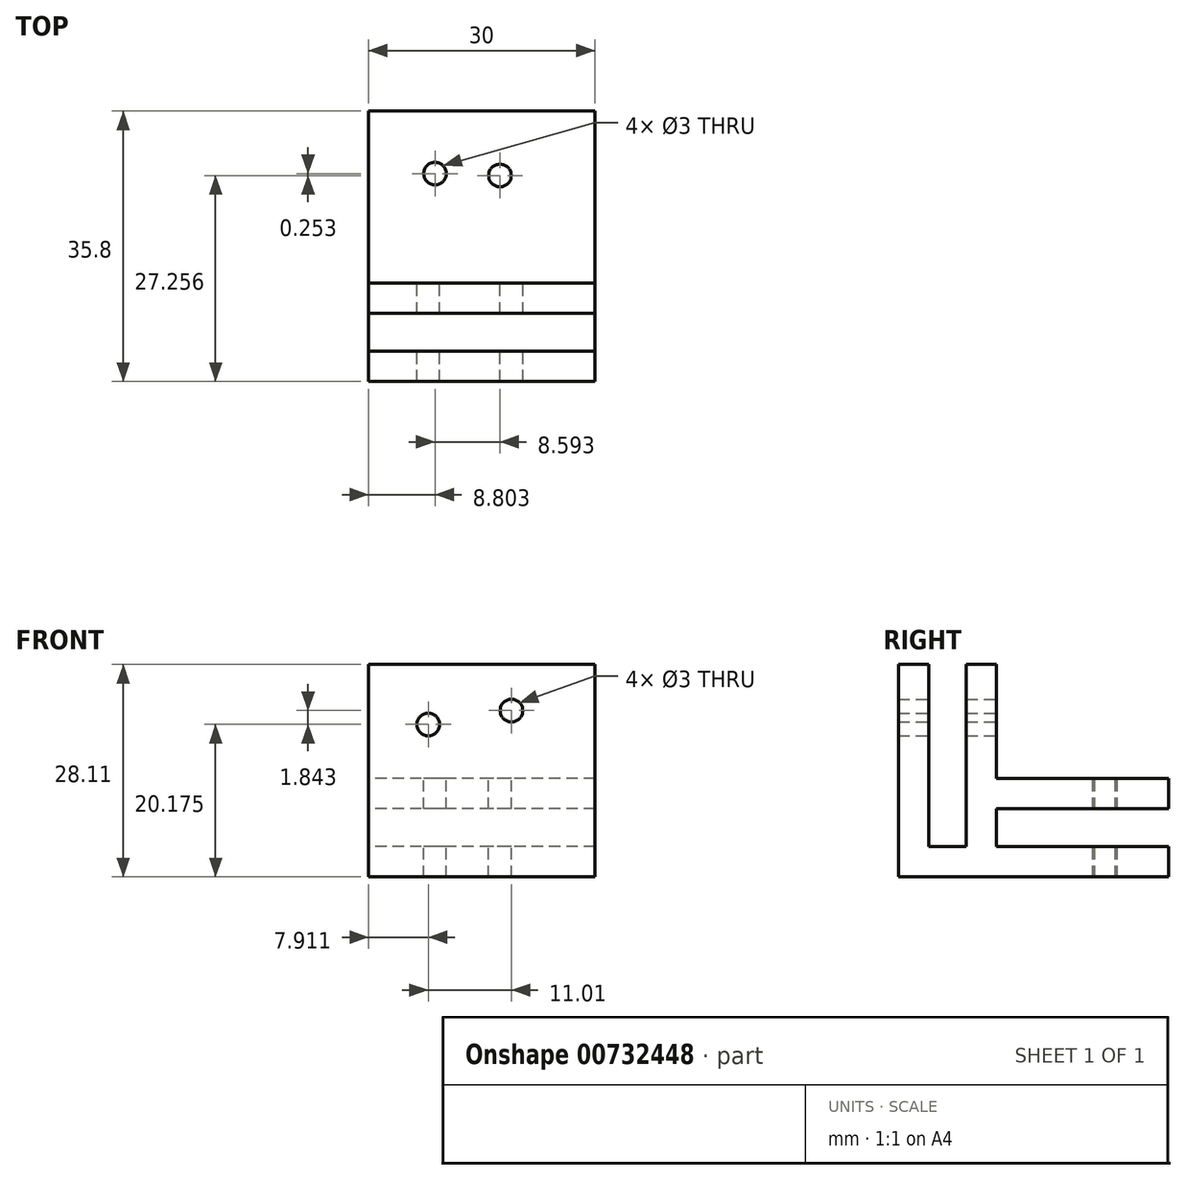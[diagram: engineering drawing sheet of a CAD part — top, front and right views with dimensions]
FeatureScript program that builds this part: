
annotation { "Feature Type Name" : "Feature", "Feature Type Description" : "" }
export const myFeature = defineFeature(function(context is Context, id is Id, definition is map)
    precondition{}
    {
        {
            var Q0;
            Q0=qCreatedBy(makeId("Right.planeOp"),FACE);
            var sketch = newSketch(context, id + "F0", { "sketchPlane" : qUnion([Q0])});
            skLineSegment(sketch, "E0.bottom", {"start": v(1.77, 0) * mm, "end": v(-16.23, 0) * mm});
            skLineSegment(sketch, "E0.top", {"start": v(1.77, -4) * mm, "end": v(-16.23, -4) * mm});
            skLineSegment(sketch, "E0.left", {"start": v(1.77, 0) * mm, "end": v(1.77, -4) * mm});
            skLineSegment(sketch, "E0.right", {"start": v(-16.23, 0) * mm, "end": v(-16.23, -4) * mm});
            skLineSegment(sketch, "E1.left", {"start": v(-16.23, 0) * mm, "end": v(-16.23, 0) * mm});
            skLineSegment(sketch, "E2.bottom", {"start": v(-16.23, 0) * mm, "end": v(-12.23, 0) * mm});
            skLineSegment(sketch, "E2.top", {"start": v(-16.23, 24.11) * mm, "end": v(-12.23, 24.11) * mm});
            skLineSegment(sketch, "E2.left", {"start": v(-16.23, 0) * mm, "end": v(-16.23, 24.11) * mm});
            skLineSegment(sketch, "E2.right", {"start": v(-12.23, 0) * mm, "end": v(-12.23, 24.11) * mm});
            skLineSegment(sketch, "E3", {"start": v(-12.23, 0) * mm, "end": v(-7.23, 0) * mm});
            skLineSegment(sketch, "E4", {"start": v(-7.23, 0) * mm, "end": v(-7.23, 25.28) * mm});
            skLineSegment(sketch, "E5", {"start": v(-7.23, 25.28) * mm, "end": v(-3.23, 25.28) * mm});
            skLineSegment(sketch, "E6", {"start": v(-3.23, 25.28) * mm, "end": v(-3.23, 0) * mm});
            skLineSegment(sketch, "E7.bottom", {"start": v(1.77, 0) * mm, "end": v(19.57, 0) * mm});
            skLineSegment(sketch, "E7.top", {"start": v(1.77, -4) * mm, "end": v(19.57, -4) * mm});
            skLineSegment(sketch, "E7.right", {"start": v(19.57, 0) * mm, "end": v(19.57, -4) * mm});
            skLineSegment(sketch, "E8", {"start": v(-7.23, 24.11) * mm, "end": v(-3.23, 24.11) * mm});
            skLineSegment(sketch, "E9", {"start": v(-3.23, 0) * mm, "end": v(-3.23, 5) * mm});
            skLineSegment(sketch, "E10", {"start": v(-3.23, 5) * mm, "end": v(19.57, 5) * mm});
            skLineSegment(sketch, "E11", {"start": v(19.57, 5) * mm, "end": v(19.57, 9) * mm});
            skLineSegment(sketch, "E12", {"start": v(19.57, 9) * mm, "end": v(-3.23, 9) * mm});
            skSolve(sketch);
        }
        {
            var Q0;
            Q0=makeQuery(id+"F0.imprint","IMPRINT",FACE,{"disambiguationData":[TD([[makeQuery(id+"F0.imprint","IMPRINT",EDGE,{"derivedFrom":sQuery(id+"F0.wireOp",EDGE,"E2.top")}),-1.0]])]});
            var Q1;
            {var subQ0=sQuery(id+"F0.wireOp",EDGE,"E10");Q1=makeQuery(id+"F0.imprint","IMPRINT",FACE,{"disambiguationData":[TD([[makeQuery(id+"F0.imprint","IMPRINT",EDGE,{"derivedFrom":subQ0}),1.0]])]});}
            var Q2;
            Q2=makeQuery(id+"F0.imprint","IMPRINT",FACE,{"disambiguationData":[TD([[makeQuery(id+"F0.imprint","IMPRINT",EDGE,{"derivedFrom":sQuery(id+"F0.wireOp",EDGE,"E0.left")}),1.0]])]});
            var Q3;
            Q3=makeQuery(id+"F0.imprint","IMPRINT",FACE,{"disambiguationData":[TD([[makeQuery(id+"F0.imprint","IMPRINT",EDGE,{"derivedFrom":sQuery(id+"F0.wireOp",EDGE,"E0.top")}),-1.0]])]});
            var Q4;
            {var subQ4=sQuery(id+"F0.wireOp",EDGE,"E8");Q4=makeQuery(id+"F0.imprint","IMPRINT",FACE,{"disambiguationData":[TD([[makeQuery(id+"F0.imprint","IMPRINT",EDGE,{"derivedFrom":subQ4}),-1.0]])]});}
            extrude(context, id + "F1", {"entities" : qUnion([Q0, Q1, Q2, Q3, Q4]), "depth" : 30 * mm, "offsetDistance" : 25 * mm});
        }
        {
            var Q0;
            {var subQ0=sQuery(id+"F0.wireOp",EDGE,"E6");Q0=makeQuery(id+"F1.opExtrude","SWEPT_FACE",FACE,{"disambiguationData":[OSD([subQ0]),TDD([makeQuery(id+"F0.imprint","IMPRINT",EDGE,{"disambiguationData":[TD([[makeQuery(id+"F0.imprint","INTERSECT",VERTEX,{"derivedFrom":[subQ0,sQuery(id+"F0.wireOp",EDGE,"E8")]}),-1.0]])],"derivedFrom":subQ0})])]});}
            var sketch = newSketch(context, id + "F2", { "sketchPlane" : qUnion([Q0])});
            skCircle(sketch, "E13", {"center": v(-18.92, 18.02) * mm, "radius": 1.5 * mm});
            skCircle(sketch, "E14", {"center": v(-7.91, 16.18) * mm, "radius": 1.5 * mm});
            skSolve(sketch);
        }
        {
            var Q0;
            Q0 = qSketchRegion(id + "F2", true);
            extrude(context, id + "F3", {"entities" : qUnion([Q0]), "operationType" : NewBodyOperationType.REMOVE, "oppositeDirection" : true, "depth" : 25 * mm, "offsetDistance" : 25 * mm});
        }
        {
            var Q0;
            Q0=makeQuery(id+"F1.opExtrude","SWEPT_FACE",FACE,{"disambiguationData":[OSD([sQuery(id+"F0.wireOp",EDGE,"E12")])]});
            var sketch = newSketch(context, id + "F4", { "sketchPlane" : qUnion([Q0])});
            skCircle(sketch, "E15", {"center": v(8.8, 11.28) * mm, "radius": 1.5 * mm});
            skCircle(sketch, "E16", {"center": v(17.4, 11.03) * mm, "radius": 1.5 * mm});
            skSolve(sketch);
        }
        {
            var Q0;
            Q0 = qSketchRegion(id + "F4", true);
            extrude(context, id + "F5", {"entities" : qUnion([Q0]), "operationType" : NewBodyOperationType.REMOVE, "oppositeDirection" : true, "depth" : 25 * mm, "offsetDistance" : 25 * mm});
        }
    });
